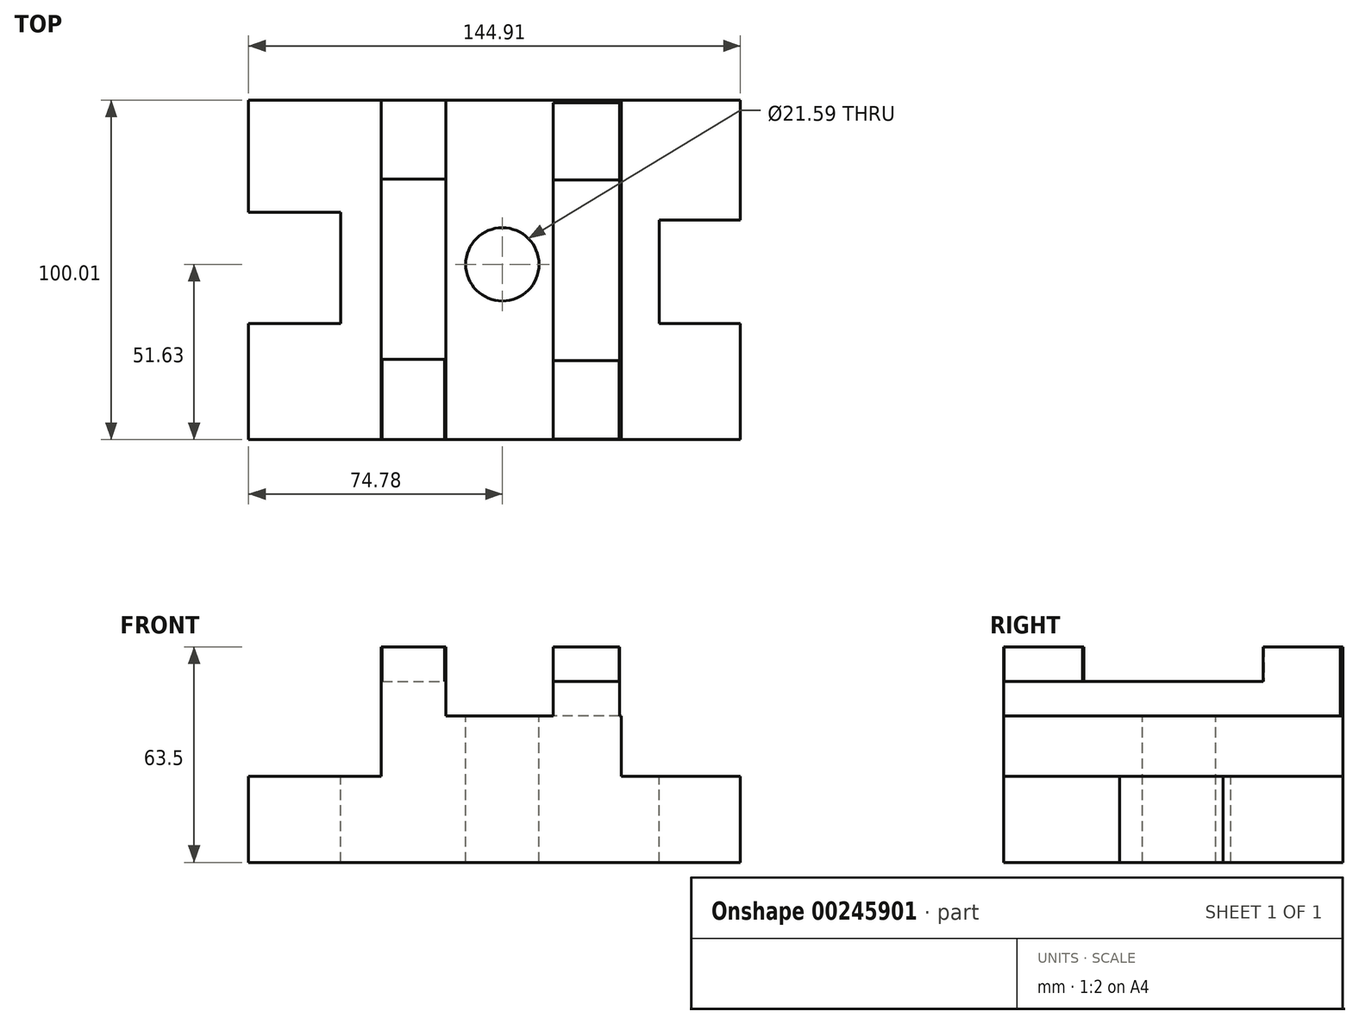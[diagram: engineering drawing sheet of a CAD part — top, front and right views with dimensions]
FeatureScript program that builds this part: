
annotation { "Feature Type Name" : "Feature", "Feature Type Description" : "" }
export const myFeature = defineFeature(function(context is Context, id is Id, definition is map)
    precondition{}
    {
        {
            var Q0;
            Q0=qCreatedBy(makeId("Top.planeOp"),FACE);
            var sketch = newSketch(context, id + "F0", { "sketchPlane" : qUnion([Q0])});
            skLineSegment(sketch, "E0.bottom", {"start": v(-74.78, 48.38) * mm, "end": v(70.13, 48.38) * mm});
            skLineSegment(sketch, "E0.top", {"start": v(-74.78, -51.63) * mm, "end": v(70.13, -51.63) * mm});
            skLineSegment(sketch, "E0.left", {"start": v(-74.78, 48.38) * mm, "end": v(-74.78, -51.63) * mm});
            skLineSegment(sketch, "E0.right", {"start": v(70.13, 48.38) * mm, "end": v(70.13, -51.63) * mm});
            skSolve(sketch);
        }
        {
            var Q0;
            Q0=makeQuery(id+"F0.imprint","IMPRINT",FACE,{"disambiguationData":[TD([[makeQuery(id+"F0.imprint","IMPRINT",EDGE,{"derivedFrom":sQuery(id+"F0.wireOp",EDGE,"E0.bottom")}),-1.0]])]});
            extrude(context, id + "F1", {"entities" : qUnion([Q0]), "depth" : 25.4 * mm});
        }
        {
            var Q0;
            Q0=makeQuery(id+"F1.opExtrude","CAP_FACE",FACE,{"disambiguationData":[OSD([sQuery(id+"F0.wireOp",EDGE,"E0.bottom"),sQuery(id+"F0.wireOp",EDGE,"E0.top"),sQuery(id+"F0.wireOp",EDGE,"E0.left"),sQuery(id+"F0.wireOp",EDGE,"E0.right")])],"isStart":false});
            var sketch = newSketch(context, id + "F2", { "sketchPlane" : qUnion([Q0])});
            skLineSegment(sketch, "E1.bottom", {"start": v(70.13, 13.02) * mm, "end": v(46.17, 13.02) * mm});
            skLineSegment(sketch, "E1.top", {"start": v(70.13, -17.44) * mm, "end": v(46.17, -17.44) * mm});
            skLineSegment(sketch, "E1.left", {"start": v(70.13, 13.02) * mm, "end": v(70.13, -17.44) * mm});
            skLineSegment(sketch, "E1.right", {"start": v(46.17, 13.02) * mm, "end": v(46.17, -17.44) * mm});
            skSolve(sketch);
        }
        {
            var Q0;
            Q0=makeQuery(id+"F2.imprint","IMPRINT",FACE,{"disambiguationData":[TD([[makeQuery(id+"F2.imprint","IMPRINT",EDGE,{"derivedFrom":sQuery(id+"F2.wireOp",EDGE,"E1.bottom")}),1.0]])]});
            extrude(context, id + "F3", {"entities" : qUnion([Q0]), "operationType" : NewBodyOperationType.REMOVE, "oppositeDirection" : true, "depth" : 25.4 * mm});
        }
        {
            var Q0;
            Q0=makeQuery(id+"F1.opExtrude","CAP_FACE",FACE,{"disambiguationData":[OSD([sQuery(id+"F0.wireOp",EDGE,"E0.bottom"),sQuery(id+"F0.wireOp",EDGE,"E0.top"),sQuery(id+"F0.wireOp",EDGE,"E0.left"),sQuery(id+"F0.wireOp",EDGE,"E0.right")])],"isStart":false});
            var sketch = newSketch(context, id + "F4", { "sketchPlane" : qUnion([Q0])});
            skLineSegment(sketch, "E2.bottom", {"start": v(-74.78, 15.35) * mm, "end": v(-47.56, 15.35) * mm});
            skLineSegment(sketch, "E2.top", {"start": v(-74.78, -17.44) * mm, "end": v(-47.56, -17.44) * mm});
            skLineSegment(sketch, "E2.left", {"start": v(-74.78, 15.35) * mm, "end": v(-74.78, -17.44) * mm});
            skLineSegment(sketch, "E2.right", {"start": v(-47.56, 15.35) * mm, "end": v(-47.56, -17.44) * mm});
            skSolve(sketch);
        }
        {
            var Q0;
            Q0=makeQuery(id+"F4.imprint","IMPRINT",FACE,{"disambiguationData":[TD([[makeQuery(id+"F4.imprint","IMPRINT",EDGE,{"derivedFrom":sQuery(id+"F4.wireOp",EDGE,"E2.bottom")}),-1.0]])]});
            extrude(context, id + "F5", {"entities" : qUnion([Q0]), "operationType" : NewBodyOperationType.REMOVE, "oppositeDirection" : true, "depth" : 25.4 * mm});
        }
        {
            var Q0;
            Q0=makeQuery(id+"F1.opExtrude","CAP_FACE",FACE,{"disambiguationData":[OSD([sQuery(id+"F0.wireOp",EDGE,"E0.bottom"),sQuery(id+"F0.wireOp",EDGE,"E0.top"),sQuery(id+"F0.wireOp",EDGE,"E0.left"),sQuery(id+"F0.wireOp",EDGE,"E0.right")])],"isStart":false});
            var sketch = newSketch(context, id + "F6", { "sketchPlane" : qUnion([Q0])});
            skLineSegment(sketch, "E3.bottom", {"start": v(35, -51.63) * mm, "end": v(-35.7, -51.63) * mm});
            skLineSegment(sketch, "E3.top", {"start": v(35, 48.38) * mm, "end": v(-35.7, 48.38) * mm});
            skLineSegment(sketch, "E3.left", {"start": v(35, -51.63) * mm, "end": v(35, 48.38) * mm});
            skLineSegment(sketch, "E3.right", {"start": v(-35.7, -51.63) * mm, "end": v(-35.7, 48.38) * mm});
            skSolve(sketch);
        }
        {
            var Q0;
            Q0=makeQuery(id+"F6.imprint","IMPRINT",FACE,{"disambiguationData":[TD([[makeQuery(id+"F6.imprint","IMPRINT",EDGE,{"derivedFrom":sQuery(id+"F6.wireOp",EDGE,"E3.bottom")}),1.0]])]});
            extrude(context, id + "F7", {"entities" : qUnion([Q0]), "operationType" : NewBodyOperationType.ADD, "depth" : 17.78 * mm});
        }
        {
            var Q0;
            Q0=makeQuery(id+"F7.opExtrude","CAP_FACE",FACE,{"disambiguationData":[OSD([sQuery(id+"F6.wireOp",EDGE,"E3.bottom"),sQuery(id+"F6.wireOp",EDGE,"E3.top"),sQuery(id+"F6.wireOp",EDGE,"E3.left"),sQuery(id+"F6.wireOp",EDGE,"E3.right")])],"isStart":false});
            var sketch = newSketch(context, id + "F8", { "sketchPlane" : qUnion([Q0])});
            skLineSegment(sketch, "E4.bottom", {"start": v(-35.7, 48.38) * mm, "end": v(-16.63, 48.38) * mm});
            skLineSegment(sketch, "E4.top", {"start": v(-35.7, -51.63) * mm, "end": v(-16.63, -51.63) * mm});
            skLineSegment(sketch, "E4.left", {"start": v(-35.7, 48.38) * mm, "end": v(-35.7, -51.63) * mm});
            skLineSegment(sketch, "E4.right", {"start": v(-16.63, 48.38) * mm, "end": v(-16.63, -51.63) * mm});
            skSolve(sketch);
        }
        {
            var Q0;
            {var subQ0=sQuery(id+"F8.wireOp",EDGE,"E4.right");Q0=makeQuery(id+"F8.imprint","IMPRINT",FACE,{"disambiguationData":[TD([[makeQuery(id+"F8.imprint","IMPRINT",EDGE,{"derivedFrom":subQ0}),1.0]])]});}
            var sketch = newSketch(context, id + "F9", { "sketchPlane" : qUnion([Q0])});
            skLineSegment(sketch, "E5.bottom", {"start": v(34.54, 47.6) * mm, "end": v(15, 47.6) * mm});
            skLineSegment(sketch, "E5.top", {"start": v(34.54, -51.73) * mm, "end": v(15, -51.73) * mm});
            skLineSegment(sketch, "E5.left", {"start": v(34.54, 47.6) * mm, "end": v(34.54, -51.73) * mm});
            skLineSegment(sketch, "E5.right", {"start": v(15, 47.6) * mm, "end": v(15, -51.73) * mm});
            skSolve(sketch);
        }
        {
            var Q0;
            {var subQ0=sQuery(id+"F9.wireOp",EDGE,"E5.bottom");Q0=makeQuery(id+"F9.imprint","IMPRINT",FACE,{"disambiguationData":[TD([[makeQuery(id+"F9.imprint","IMPRINT",EDGE,{"derivedFrom":subQ0}),1.0]])]});}
            var Q1;
            Q1=makeQuery(id+"F8.imprint","IMPRINT",FACE,{"disambiguationData":[TD([[makeQuery(id+"F8.imprint","IMPRINT",EDGE,{"derivedFrom":sQuery(id+"F8.wireOp",EDGE,"E4.bottom")}),-1.0]])]});
            extrude(context, id + "F10", {"entities" : qUnion([Q0, Q1]), "operationType" : NewBodyOperationType.ADD, "depth" : 10.16 * mm});
        }
        {
            var Q0;
            Q0=makeQuery(id+"F10.opExtrude","CAP_FACE",FACE,{"disambiguationData":[OSD([sQuery(id+"F8.wireOp",EDGE,"E4.bottom"),sQuery(id+"F8.wireOp",EDGE,"E4.top"),sQuery(id+"F8.wireOp",EDGE,"E4.left"),sQuery(id+"F8.wireOp",EDGE,"E4.right")])],"isStart":false});
            var sketch = newSketch(context, id + "F11", { "sketchPlane" : qUnion([Q0])});
            skLineSegment(sketch, "E6.bottom", {"start": v(-35.7, 48.38) * mm, "end": v(-16.63, 48.38) * mm});
            skLineSegment(sketch, "E6.top", {"start": v(-35.7, 25.09) * mm, "end": v(-16.63, 25.09) * mm});
            skLineSegment(sketch, "E6.left", {"start": v(-35.7, 48.38) * mm, "end": v(-35.7, 25.09) * mm});
            skLineSegment(sketch, "E6.right", {"start": v(-16.63, 48.38) * mm, "end": v(-16.63, 25.09) * mm});
            skSolve(sketch);
        }
        {
            var Q0;
            Q0=makeQuery(id+"F10.opExtrude","CAP_FACE",FACE,{"disambiguationData":[OSD([sQuery(id+"F6.wireOp",EDGE,"E3.bottom"),sQuery(id+"F9.wireOp",EDGE,"E5.bottom"),sQuery(id+"F9.wireOp",EDGE,"E5.left"),sQuery(id+"F9.wireOp",EDGE,"E5.right")])],"isStart":false});
            var sketch = newSketch(context, id + "F12", { "sketchPlane" : qUnion([Q0])});
            skLineSegment(sketch, "E7.bottom", {"start": v(15, 47.6) * mm, "end": v(34.54, 47.6) * mm});
            skLineSegment(sketch, "E7.top", {"start": v(15, 24.85) * mm, "end": v(34.54, 24.85) * mm});
            skLineSegment(sketch, "E7.left", {"start": v(15, 47.6) * mm, "end": v(15, 24.85) * mm});
            skLineSegment(sketch, "E7.right", {"start": v(34.54, 47.6) * mm, "end": v(34.54, 24.85) * mm});
            skSolve(sketch);
        }
        {
            var Q0;
            {var subQ0=sQuery(id+"F11.wireOp",EDGE,"E6.top");Q0=makeQuery(id+"F11.imprint","IMPRINT",FACE,{"disambiguationData":[TD([[makeQuery(id+"F11.imprint","IMPRINT",EDGE,{"derivedFrom":subQ0}),-1.0]])]});}
            var sketch = newSketch(context, id + "F13", { "sketchPlane" : qUnion([Q0])});
            skLineSegment(sketch, "E8.bottom", {"start": v(-35.4, -51.9) * mm, "end": v(-17.03, -51.9) * mm});
            skLineSegment(sketch, "E8.top", {"start": v(-35.4, -27.94) * mm, "end": v(-17.03, -27.94) * mm});
            skLineSegment(sketch, "E8.left", {"start": v(-35.4, -51.9) * mm, "end": v(-35.4, -27.94) * mm});
            skLineSegment(sketch, "E8.right", {"start": v(-17.03, -51.9) * mm, "end": v(-17.03, -27.94) * mm});
            skSolve(sketch);
        }
        {
            var Q0;
            {var subQ0=sQuery(id+"F12.wireOp",EDGE,"E7.top");Q0=makeQuery(id+"F12.imprint","IMPRINT",FACE,{"disambiguationData":[TD([[makeQuery(id+"F12.imprint","IMPRINT",EDGE,{"derivedFrom":subQ0}),-1.0]])]});}
            var sketch = newSketch(context, id + "F14", { "sketchPlane" : qUnion([Q0])});
            skLineSegment(sketch, "E9.bottom", {"start": v(14.83, -51.43) * mm, "end": v(34.37, -51.43) * mm});
            skLineSegment(sketch, "E9.top", {"start": v(14.83, -28.4) * mm, "end": v(34.37, -28.4) * mm});
            skLineSegment(sketch, "E9.left", {"start": v(14.83, -51.43) * mm, "end": v(14.83, -28.4) * mm});
            skLineSegment(sketch, "E9.right", {"start": v(34.37, -51.43) * mm, "end": v(34.37, -28.4) * mm});
            skSolve(sketch);
        }
        {
            var Q0;
            Q0=makeQuery(id+"F12.imprint","IMPRINT",FACE,{"disambiguationData":[TD([[makeQuery(id+"F12.imprint","IMPRINT",EDGE,{"derivedFrom":sQuery(id+"F12.wireOp",EDGE,"E7.bottom")}),1.0]])]});
            var Q1;
            Q1=makeQuery(id+"F11.imprint","IMPRINT",FACE,{"disambiguationData":[TD([[makeQuery(id+"F11.imprint","IMPRINT",EDGE,{"derivedFrom":sQuery(id+"F11.wireOp",EDGE,"E6.bottom")}),-1.0]])]});
            extrude(context, id + "F15", {"entities" : qUnion([Q0, Q1]), "operationType" : NewBodyOperationType.ADD, "depth" : 10.16 * mm});
        }
        {
            var Q0;
            {var subQ0=sQuery(id+"F13.wireOp",EDGE,"E8.top");Q0=makeQuery(id+"F13.imprint","IMPRINT",FACE,{"disambiguationData":[TD([[makeQuery(id+"F13.imprint","IMPRINT",EDGE,{"derivedFrom":subQ0}),-1.0]])]});}
            var Q1;
            {var subQ0=sQuery(id+"F14.wireOp",EDGE,"E9.right");Q1=makeQuery(id+"F14.imprint","IMPRINT",FACE,{"disambiguationData":[TD([[makeQuery(id+"F14.imprint","IMPRINT",EDGE,{"derivedFrom":subQ0}),1.0]])]});}
            extrude(context, id + "F16", {"entities" : qUnion([Q0, Q1]), "operationType" : NewBodyOperationType.ADD, "depth" : 10.16 * mm});
        }
        {
            var Q0;
            Q0=makeQuery(id+"F7.opExtrude","CAP_FACE",FACE,{"disambiguationData":[OSD([sQuery(id+"F6.wireOp",EDGE,"E3.bottom"),sQuery(id+"F6.wireOp",EDGE,"E3.top"),sQuery(id+"F6.wireOp",EDGE,"E3.left"),sQuery(id+"F6.wireOp",EDGE,"E3.right")])],"isStart":false});
            var sketch = newSketch(context, id + "F17", { "sketchPlane" : qUnion([Q0])});
            skCircle(sketch, "E10", {"center": v(0, 0) * mm, "radius": 11.05 * mm});
            skSolve(sketch);
        }
        {
            var Q0;
            Q0=makeQuery(id+"F17.imprint","IMPRINT",FACE,{"disambiguationData":[TD([[makeQuery(id+"F17.imprint","IMPRINT",EDGE,{"derivedFrom":sQuery(id+"F17.wireOp",EDGE,"E10")}),-1.0]])]});
            var sketch = newSketch(context, id + "F18", { "sketchPlane" : qUnion([Q0])});
            skLineSegment(sketch, "E11", {"start": v(0, 0) * mm, "end": v(0, 33.7) * mm});
            skLineSegment(sketch, "E12", {"start": v(0, 0) * mm, "end": v(0, -50.04) * mm});
            skLineSegment(sketch, "E13", {"start": v(0, 0) * mm, "end": v(-76.57, 0) * mm});
            skLineSegment(sketch, "E14", {"start": v(0, 0) * mm, "end": v(60.88, 0) * mm});
            skSolve(sketch);
        }
        {
            var Q0;
            Q0=sQuery(id+"F18.wireOp",VERTEX,"E11.start");
            var Q1;
            Q1=makeQuery(id+"F1.opExtrude","SWEPT_BODY",BODY,{"disambiguationData":[OSD([sQuery(id+"F0.wireOp",EDGE,"E0.bottom"),sQuery(id+"F0.wireOp",EDGE,"E0.top"),sQuery(id+"F0.wireOp",EDGE,"E0.left"),sQuery(id+"F0.wireOp",EDGE,"E0.right")])]});
            hole(context, id + "F19", {"style" : HoleStyle.SIMPLE, "endStyle" : HoleEndStyle.THROUGH, "holeDiameter" : 21.59 * mm, "tappedDepth" : 12.7 * mm, "tapClearance" : 3, "locations" : qUnion([Q0]), "scope" : qUnion([Q1])});
        }
    });
